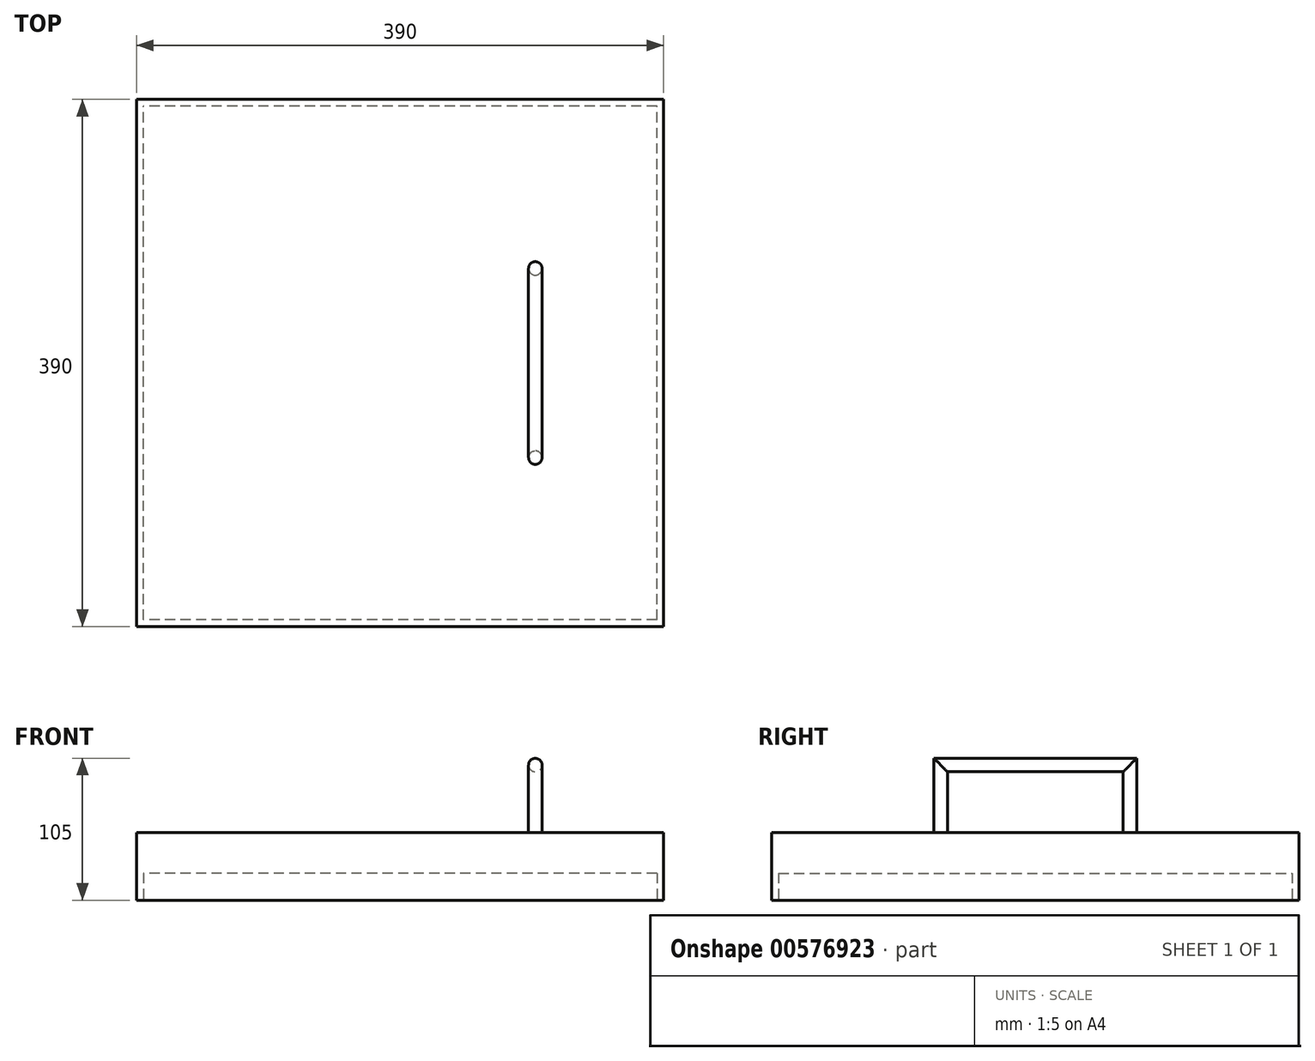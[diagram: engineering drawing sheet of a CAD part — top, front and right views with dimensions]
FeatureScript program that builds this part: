
annotation { "Feature Type Name" : "Feature", "Feature Type Description" : "" }
export const myFeature = defineFeature(function(context is Context, id is Id, definition is map)
    precondition{}
    {
        {
            var Q0;
            Q0=qCreatedBy(makeId("Top.planeOp"),FACE);
            var sketch = newSketch(context, id + "F0", { "sketchPlane" : qUnion([Q0])});
            skLineSegment(sketch, "E0.bottom", {"start": v(195, 195) * mm, "end": v(-195, 195) * mm});
            skLineSegment(sketch, "E0.top", {"start": v(195, -195) * mm, "end": v(-195, -195) * mm});
            skLineSegment(sketch, "E0.left", {"start": v(195, 195) * mm, "end": v(195, -195) * mm});
            skLineSegment(sketch, "E0.right", {"start": v(-195, 195) * mm, "end": v(-195, -195) * mm});
            skPoint(sketch, "E0.middle", {"position": v(0, 0) * mm});
            skSolve(sketch);
        }
        {
            var Q0;
            Q0 = qSketchRegion(id + "F0", true);
            extrude(context, id + "F1", {"entities" : qUnion([Q0]), "depth" : 50 * mm, "offsetDistance" : 25 * mm});
        }
        {
            var Q0;
            Q0=makeQuery(id+"F1.opExtrude","CAP_FACE",FACE,{"disambiguationData":[OSD([sQuery(id+"F0.wireOp",EDGE,"E0.bottom"),sQuery(id+"F0.wireOp",EDGE,"E0.top"),sQuery(id+"F0.wireOp",EDGE,"E0.left"),sQuery(id+"F0.wireOp",EDGE,"E0.right")])],"isStart":true});
            var sketch = newSketch(context, id + "F2", { "sketchPlane" : qUnion([Q0])});
            skLineSegment(sketch, "E1.bottom", {"start": v(190, 190) * mm, "end": v(-190, 190) * mm});
            skLineSegment(sketch, "E1.top", {"start": v(190, -190) * mm, "end": v(-190, -190) * mm});
            skLineSegment(sketch, "E1.left", {"start": v(190, 190) * mm, "end": v(190, -190) * mm});
            skLineSegment(sketch, "E1.right", {"start": v(-190, 190) * mm, "end": v(-190, -190) * mm});
            skPoint(sketch, "E1.middle", {"position": v(0, 0) * mm});
            skSolve(sketch);
        }
        {
            var Q0;
            Q0 = qSketchRegion(id + "F2", true);
            extrude(context, id + "F3", {"entities" : qUnion([Q0]), "operationType" : NewBodyOperationType.REMOVE, "oppositeDirection" : true, "depth" : 20 * mm, "offsetDistance" : 25 * mm});
        }
        {
            var Q0;
            Q0=qCreatedBy(makeId("Right.planeOp"),FACE);
            cPlane(context, id + "F4", {"entities" : qUnion([Q0]), "cplaneType" : CPlaneType.OFFSET, "offset" : 100 * mm, "width" : 150 * mm, "height" : 150 * mm});
        }
        {
            var Q0;
            Q0=qCreatedBy(id+"F4.planeOp",FACE);
            var sketch = newSketch(context, id + "F5", { "sketchPlane" : qUnion([Q0])});
            skLineSegment(sketch, "E2", {"start": v(70, 50) * mm, "end": v(70, 100) * mm});
            skLineSegment(sketch, "E3", {"start": v(70, 100) * mm, "end": v(-70, 100) * mm});
            skLineSegment(sketch, "E4", {"start": v(-70, 100) * mm, "end": v(-70, 50) * mm});
            skLineSegment(sketch, "E5", {"start": v(195, 50) * mm, "end": v(70, 50) * mm, "construction": true});
            skLineSegment(sketch, "E6", {"start": v(-70, 50) * mm, "end": v(-195, 50) * mm, "construction": true});
            skSolve(sketch);
        }
        {
            var Q0;
            Q0=makeQuery(id+"F1.opExtrude","CAP_FACE",FACE,{"disambiguationData":[OSD([sQuery(id+"F0.wireOp",EDGE,"E0.bottom"),sQuery(id+"F0.wireOp",EDGE,"E0.top"),sQuery(id+"F0.wireOp",EDGE,"E0.left"),sQuery(id+"F0.wireOp",EDGE,"E0.right")])],"isStart":false});
            var sketch = newSketch(context, id + "F6", { "sketchPlane" : qUnion([Q0])});
            skPoint(sketch, "E7.0", {"position": v(100, 70) * mm});
            skCircle(sketch, "E8", {"center": v(100, 70) * mm, "radius": 5 * mm});
            skSolve(sketch);
        }
        {
            var Q0;
            Q0=makeQuery(id+"F6.imprint","IMPRINT",FACE,{"disambiguationData":[TD([[makeQuery(id+"F6.imprint","IMPRINT",EDGE,{"derivedFrom":sQuery(id+"F6.wireOp",EDGE,"E8")}),1.0]])]});
            var Q1;
            Q1=sQuery(id+"F5.wireOp",EDGE,"E2");
            var Q2;
            Q2=sQuery(id+"F5.wireOp",EDGE,"E3");
            var Q3;
            Q3=sQuery(id+"F5.wireOp",EDGE,"E4");
            sweep(context, id + "F7", {"operationType" : NewBodyOperationType.ADD, "profiles" : qUnion([Q0]), "path" : qUnion([Q1, Q2, Q3])});
        }
    });
